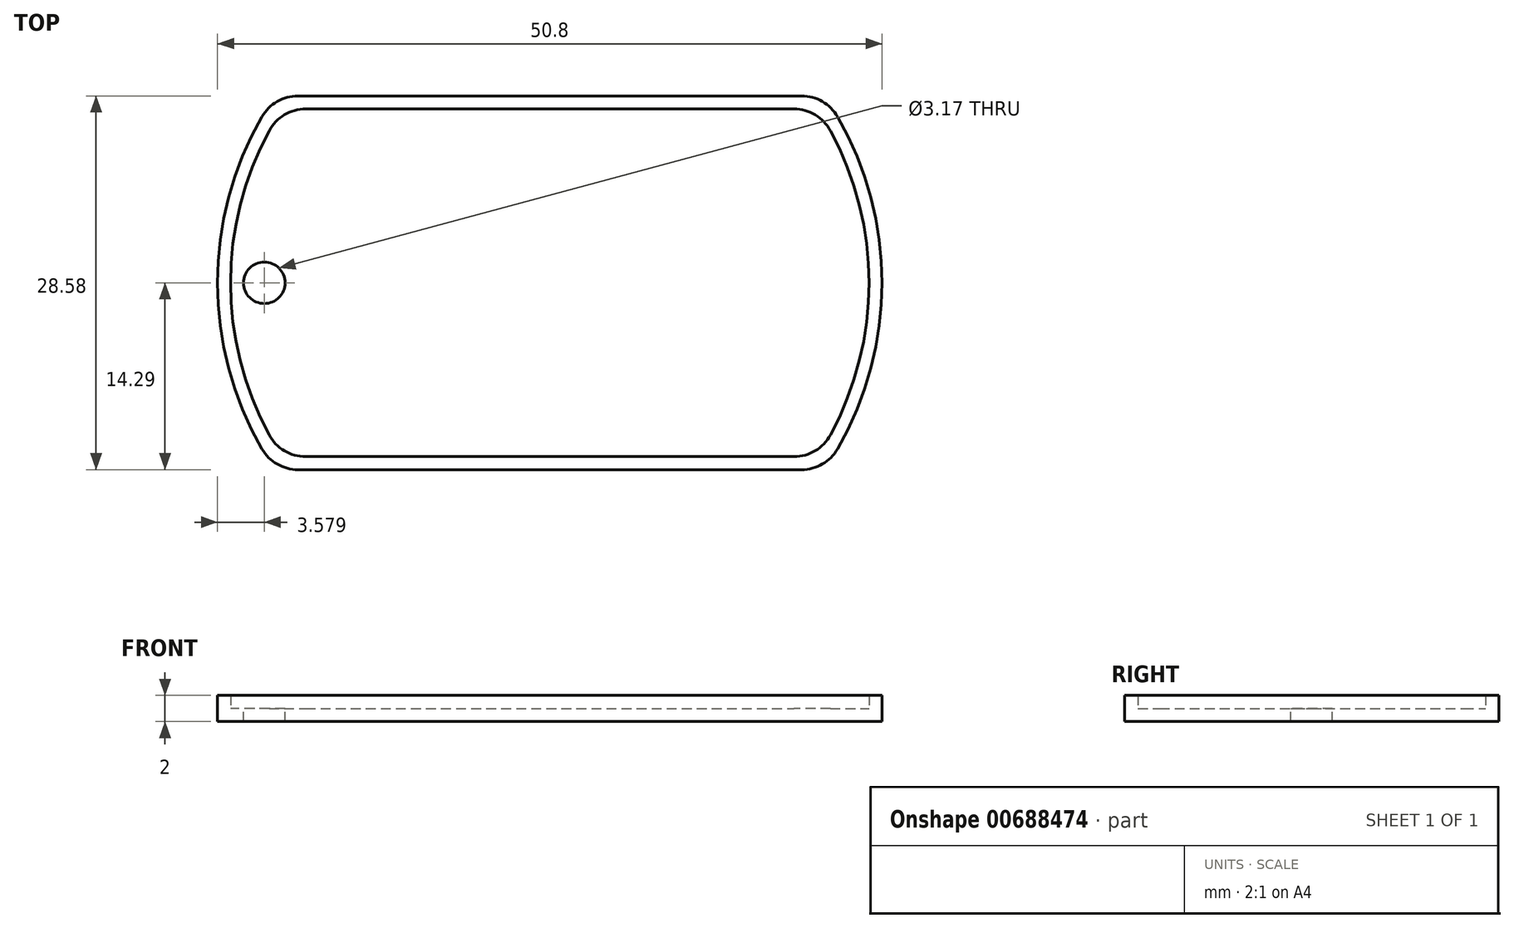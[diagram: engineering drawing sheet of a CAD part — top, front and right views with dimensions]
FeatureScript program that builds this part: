
annotation { "Feature Type Name" : "Feature", "Feature Type Description" : "" }
export const myFeature = defineFeature(function(context is Context, id is Id, definition is map)
    precondition{}
    {
        {
            var Q0;
            Q0=qCreatedBy(makeId("Top.planeOp"),FACE);
            var sketch = newSketch(context, id + "F0", { "sketchPlane" : qUnion([Q0])});
            skArc(sketch, "E0", {"start": v(-22, 12.7) * mm, "mid": v(-25.4, 0) * mm, "end": v(-22, -12.7) * mm});
            skLineSegment(sketch, "E1.top", {"start": v(-19.25, -14.29) * mm, "end": v(19.25, -14.29) * mm});
            skArc(sketch, "E2.trimOffspring", {"start": v(22, -12.7) * mm, "mid": v(25.4, 0) * mm, "end": v(22, 12.7) * mm});
            skLineSegment(sketch, "E3", {"start": v(-19.25, 14.29) * mm, "end": v(19.25, 14.29) * mm});
            skPoint(sketch, "E4.visualSharp", {"position": v(-21, 14.29) * mm});
            skArc(sketch, "E4.filletArc", {"start": v(-19.25, 14.29) * mm, "mid": v(-20.83, 13.86) * mm, "end": v(-22, 12.7) * mm});
            skPoint(sketch, "E5.visualSharp", {"position": v(21, 14.29) * mm});
            skArc(sketch, "E5.filletArc", {"start": v(22, 12.7) * mm, "mid": v(20.83, 13.86) * mm, "end": v(19.25, 14.29) * mm});
            skPoint(sketch, "E6.visualSharp", {"position": v(21, -14.29) * mm});
            skArc(sketch, "E6.filletArc", {"start": v(19.25, -14.29) * mm, "mid": v(20.83, -13.86) * mm, "end": v(22, -12.7) * mm});
            skPoint(sketch, "E7.visualSharp", {"position": v(-21, -14.29) * mm});
            skArc(sketch, "E7.filletArc", {"start": v(-22, -12.7) * mm, "mid": v(-20.83, -13.86) * mm, "end": v(-19.25, -14.29) * mm});
            skSolve(sketch);
        }
        {
            var Q0;
            Q0=makeQuery(id+"F0.imprint","IMPRINT",FACE,{"disambiguationData":[TD([[makeQuery(id+"F0.imprint","IMPRINT",EDGE,{"derivedFrom":sQuery(id+"F0.wireOp",EDGE,"E0")}),1.0]])]});
            extrude(context, id + "F1", {"entities" : qUnion([Q0]), "depth" : 1 * mm, "offsetDistance" : 25.4 * mm});
        }
        {
            var Q0;
            Q0=makeQuery(id+"F1.opExtrude","CAP_FACE",FACE,{"disambiguationData":[OSD([sQuery(id+"F0.wireOp",EDGE,"E0"),sQuery(id+"F0.wireOp",EDGE,"E1.top"),sQuery(id+"F0.wireOp",EDGE,"E2.trimOffspring"),sQuery(id+"F0.wireOp",EDGE,"E3"),sQuery(id+"F0.wireOp",EDGE,"E4.filletArc"),sQuery(id+"F0.wireOp",EDGE,"E5.filletArc"),sQuery(id+"F0.wireOp",EDGE,"E6.filletArc"),sQuery(id+"F0.wireOp",EDGE,"E7.filletArc")])],"isStart":false});
            var sketch = newSketch(context, id + "F2", { "sketchPlane" : qUnion([Q0])});
            skLineSegment(sketch, "E8.0", {"start": v(-18.66, 13.29) * mm, "end": v(18.66, 13.29) * mm});
            skArc(sketch, "E8.1", {"start": v(-21.45, 11.63) * mm, "mid": v(-24.4, 0) * mm, "end": v(-21.45, -11.63) * mm});
            skLineSegment(sketch, "E8.2", {"start": v(-18.66, -13.29) * mm, "end": v(18.66, -13.29) * mm});
            skArc(sketch, "E8.3", {"start": v(21.45, -11.63) * mm, "mid": v(24.4, 0) * mm, "end": v(21.45, 11.63) * mm});
            skPoint(sketch, "E9.visualSharp", {"position": v(-20.46, 13.29) * mm});
            skArc(sketch, "E9.filletArc", {"start": v(-18.66, 13.29) * mm, "mid": v(-20.29, 12.84) * mm, "end": v(-21.45, 11.63) * mm});
            skPoint(sketch, "E10.visualSharp", {"position": v(20.46, 13.29) * mm});
            skArc(sketch, "E10.filletArc", {"start": v(21.45, 11.63) * mm, "mid": v(20.29, 12.84) * mm, "end": v(18.66, 13.29) * mm});
            skPoint(sketch, "E11.visualSharp", {"position": v(20.46, -13.29) * mm});
            skArc(sketch, "E11.filletArc", {"start": v(18.66, -13.29) * mm, "mid": v(20.29, -12.84) * mm, "end": v(21.45, -11.63) * mm});
            skPoint(sketch, "E12.visualSharp", {"position": v(-20.46, -13.29) * mm});
            skArc(sketch, "E12.filletArc", {"start": v(-21.45, -11.63) * mm, "mid": v(-20.29, -12.84) * mm, "end": v(-18.66, -13.29) * mm});
            skLineSegment(sketch, "E13.0", {"start": v(-19.25, 14.29) * mm, "end": v(19.25, 14.29) * mm});
            skArc(sketch, "E13.1", {"start": v(-22, 12.7) * mm, "mid": v(-25.4, 0) * mm, "end": v(-22, -12.7) * mm});
            skLineSegment(sketch, "E13.2", {"start": v(-19.25, -14.29) * mm, "end": v(19.25, -14.29) * mm});
            skArc(sketch, "E13.3", {"start": v(22, -12.7) * mm, "mid": v(25.4, 0) * mm, "end": v(22, 12.7) * mm});
            skPoint(sketch, "E14.visualSharp", {"position": v(-21, -14.29) * mm});
            skArc(sketch, "E14.filletArc", {"start": v(-22, -12.7) * mm, "mid": v(-20.83, -13.86) * mm, "end": v(-19.25, -14.29) * mm});
            skPoint(sketch, "E15.visualSharp", {"position": v(21, -14.29) * mm});
            skArc(sketch, "E15.filletArc", {"start": v(19.25, -14.29) * mm, "mid": v(20.83, -13.86) * mm, "end": v(22, -12.7) * mm});
            skPoint(sketch, "E16.visualSharp", {"position": v(21, 14.29) * mm});
            skArc(sketch, "E16.filletArc", {"start": v(22, 12.7) * mm, "mid": v(20.83, 13.86) * mm, "end": v(19.25, 14.29) * mm});
            skPoint(sketch, "E17.visualSharp", {"position": v(-21, 14.29) * mm});
            skArc(sketch, "E17.filletArc", {"start": v(-19.25, 14.29) * mm, "mid": v(-20.83, 13.86) * mm, "end": v(-22, 12.7) * mm});
            skSolve(sketch);
        }
        {
            var Q0;
            Q0=makeQuery(id+"F2.imprint","IMPRINT",FACE,{"disambiguationData":[TD([[makeQuery(id+"F2.imprint","IMPRINT",EDGE,{"derivedFrom":sQuery(id+"F2.wireOp",EDGE,"E8.0")}),1.0]])]});
            extrude(context, id + "F3", {"entities" : qUnion([Q0]), "operationType" : NewBodyOperationType.ADD, "depth" : 1 * mm, "offsetDistance" : 25.4 * mm});
        }
        {
            var Q0;
            Q0=makeQuery(id+"F1.opExtrude","CAP_FACE",FACE,{"disambiguationData":[OSD([sQuery(id+"F0.wireOp",EDGE,"E0"),sQuery(id+"F0.wireOp",EDGE,"E1.top"),sQuery(id+"F0.wireOp",EDGE,"E2.trimOffspring"),sQuery(id+"F0.wireOp",EDGE,"E3"),sQuery(id+"F0.wireOp",EDGE,"E4.filletArc"),sQuery(id+"F0.wireOp",EDGE,"E5.filletArc"),sQuery(id+"F0.wireOp",EDGE,"E6.filletArc"),sQuery(id+"F0.wireOp",EDGE,"E7.filletArc")])],"isStart":false});
            var sketch = newSketch(context, id + "F4", { "sketchPlane" : qUnion([Q0])});
            skCircle(sketch, "E18", {"center": v(-21.82, 0) * mm, "radius": 1.59 * mm});
            skSolve(sketch);
        }
        {
            var Q0;
            Q0=makeQuery(id+"F4.imprint","IMPRINT",FACE,{"disambiguationData":[TD([[makeQuery(id+"F4.imprint","IMPRINT",EDGE,{"derivedFrom":sQuery(id+"F4.wireOp",EDGE,"E18")}),1.0]])]});
            extrude(context, id + "F5", {"entities" : qUnion([Q0]), "operationType" : NewBodyOperationType.REMOVE, "oppositeDirection" : true, "depth" : 1 * mm, "offsetDistance" : 25.4 * mm});
        }
        {
            var Q0;
            Q0=makeQuery(id+"F2.imprint","IMPRINT",FACE,{"disambiguationData":[TD([[makeQuery(id+"F2.imprint","IMPRINT",EDGE,{"derivedFrom":sQuery(id+"F2.wireOp",EDGE,"E8.0")}),-1.0]])]});
            var sketch = newSketch(context, id + "F6", { "sketchPlane" : qUnion([Q0])});
            skText(sketch, "E19", { "text": "Abdishakur", "fontName": "OpenSans-Regular.ttf"});
            const initialGuessF6  = {"E19": [-0.01974, 0.0036, 1, 0, 0.00545]};
            skSetInitialGuess(sketch, initialGuessF6);
            skSolve(sketch);
        }
        {
            var Q0;
            Q0=makeQuery(id+"F2.imprint","IMPRINT",FACE,{"disambiguationData":[TD([[makeQuery(id+"F2.imprint","IMPRINT",EDGE,{"derivedFrom":sQuery(id+"F2.wireOp",EDGE,"E8.0")}),-1.0]])]});
            var sketch = newSketch(context, id + "F7", { "sketchPlane" : qUnion([Q0])});
            skText(sketch, "E20", { "text": "Mire", "fontName": "OpenSans-Regular.ttf"});
            const initialGuessF7  = {"E20": [-0.01002, -0.00636, 1, 0, 0.00636]};
            skSetInitialGuess(sketch, initialGuessF7);
            skSolve(sketch);
        }
        {
            var Q0;
            Q0=makeQuery(id+"F2.imprint","IMPRINT",FACE,{"disambiguationData":[TD([[makeQuery(id+"F2.imprint","IMPRINT",EDGE,{"derivedFrom":sQuery(id+"F2.wireOp",EDGE,"E8.0")}),-1.0]])]});
            var sketch = newSketch(context, id + "F8", { "sketchPlane" : qUnion([Q0])});
            skText(sketch, "E21", { "text": "Nov. 14, 1999", "fontName": "OpenSans-Regular.ttf"});
            const initialGuessF8  = {"E21": [-0.02045, -0.01134, 1, 0, 0.00308]};
            skSetInitialGuess(sketch, initialGuessF8);
            skSolve(sketch);
        }
        {
            var Q0;
            Q0=makeQuery(id+"F2.imprint","IMPRINT",FACE,{"disambiguationData":[TD([[makeQuery(id+"F2.imprint","IMPRINT",EDGE,{"derivedFrom":sQuery(id+"F2.wireOp",EDGE,"E8.0")}),-1.0]])]});
            var sketch = newSketch(context, id + "F9", { "sketchPlane" : qUnion([Q0])});
            skText(sketch, "E22", { "text": "ATM", "fontName": "OpenSans-Regular.ttf"});
            const initialGuessF9  = {"E22": [0.008, -0.01134, 1, 0, 0.00308]};
            skSetInitialGuess(sketch, initialGuessF9);
            skSolve(sketch);
        }
        {
            var Q0;
            Q0 = qConstructionFilter(qBodyType(qCreatedBy(id + "F6" ,EDGE), BodyType.WIRE), ConstructionObject.NO);
            var Q1;
            Q1 = qConstructionFilter(qBodyType(qCreatedBy(id + "F7" ,EDGE), BodyType.WIRE), ConstructionObject.NO);
            var Q2;
            Q2 = qConstructionFilter(qBodyType(qCreatedBy(id + "F8" ,EDGE), BodyType.WIRE), ConstructionObject.NO);
            var Q3;
            Q3 = qConstructionFilter(qBodyType(qCreatedBy(id + "F9" ,EDGE), BodyType.WIRE), ConstructionObject.NO);
            extrude(context, id + "F10", {"bodyType" : ToolBodyType.SURFACE, "surfaceEntities" : qUnion([Q0, Q1, Q2, Q3]), "depth" : 1 * mm, "offsetDistance" : 25.4 * mm});
        }
    });
